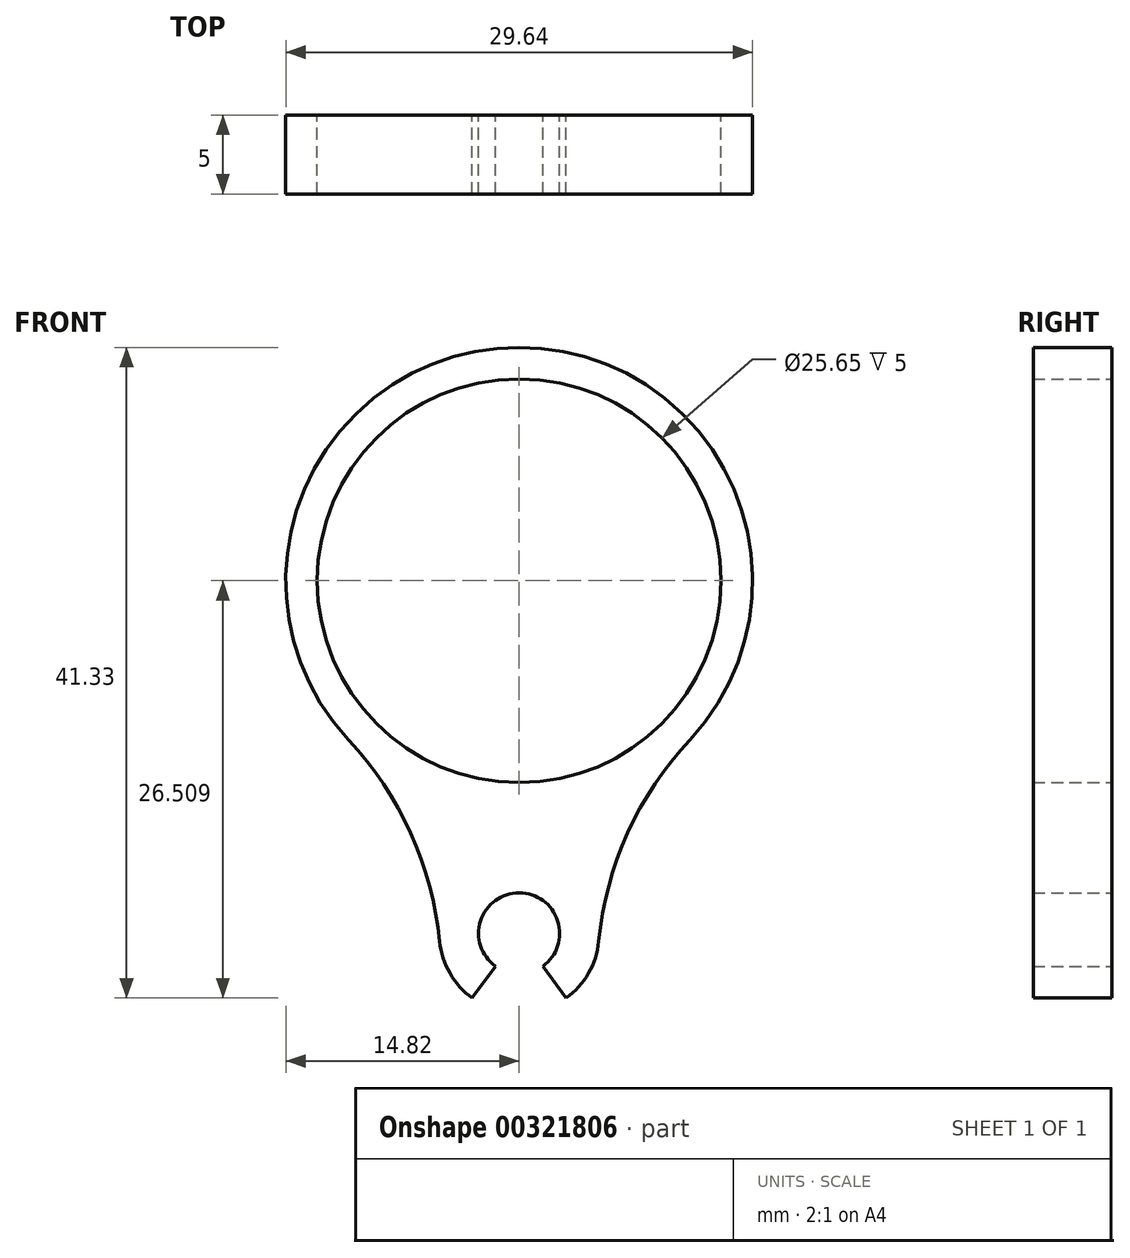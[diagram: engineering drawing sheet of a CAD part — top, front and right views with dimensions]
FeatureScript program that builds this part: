
annotation { "Feature Type Name" : "Feature", "Feature Type Description" : "" }
export const myFeature = defineFeature(function(context is Context, id is Id, definition is map)
    precondition{}
    {
        {
            var Q0;
            Q0=qCreatedBy(makeId("Front.planeOp"),FACE);
            var sketch = newSketch(context, id + "F0", { "sketchPlane" : qUnion([Q0])});
            skCircle(sketch, "E0", {"center": v(0, 19.68) * mm, "radius": 12.82 * mm});
            skArc(sketch, "E1", {"start": v(1.51, -4.8) * mm, "mid": v(0, -0.15) * mm, "end": v(-1.51, -4.8) * mm});
            skArc(sketch, "E2.0", {"start": v(10.84, 9.56) * mm, "mid": v(0, 34.5) * mm, "end": v(-10.84, 9.56) * mm});
            skArc(sketch, "E3.0", {"start": v(-5.05, -3.22) * mm, "mid": v(-4.4, -5.25) * mm, "end": v(-2.98, -6.83) * mm});
            skArc(sketch, "E4", {"start": v(-5.05, -3.22) * mm, "mid": v(-6.9, 3.65) * mm, "end": v(-10.84, 9.56) * mm});
            skArc(sketch, "E5", {"start": v(10.84, 9.56) * mm, "mid": v(6.9, 3.65) * mm, "end": v(5.05, -3.22) * mm});
            skLineSegment(sketch, "E6", {"start": v(-1.51, -4.8) * mm, "end": v(-2.98, -6.83) * mm});
            skLineSegment(sketch, "E7", {"start": v(1.51, -4.8) * mm, "end": v(2.98, -6.83) * mm});
            skArc(sketch, "E8.trimOffspring", {"start": v(2.98, -6.83) * mm, "mid": v(4.4, -5.25) * mm, "end": v(5.05, -3.22) * mm});
            skSolve(sketch);
        }
        {
            var Q0;
            Q0=makeQuery(id+"F0.imprint","IMPRINT",FACE,{"disambiguationData":[TD([[makeQuery(id+"F0.imprint","IMPRINT",EDGE,{"derivedFrom":sQuery(id+"F0.wireOp",EDGE,"E0")}),-1.0]])]});
            extrude(context, id + "F1", {"entities" : qUnion([Q0]), "depth" : 5 * mm});
        }
    });
